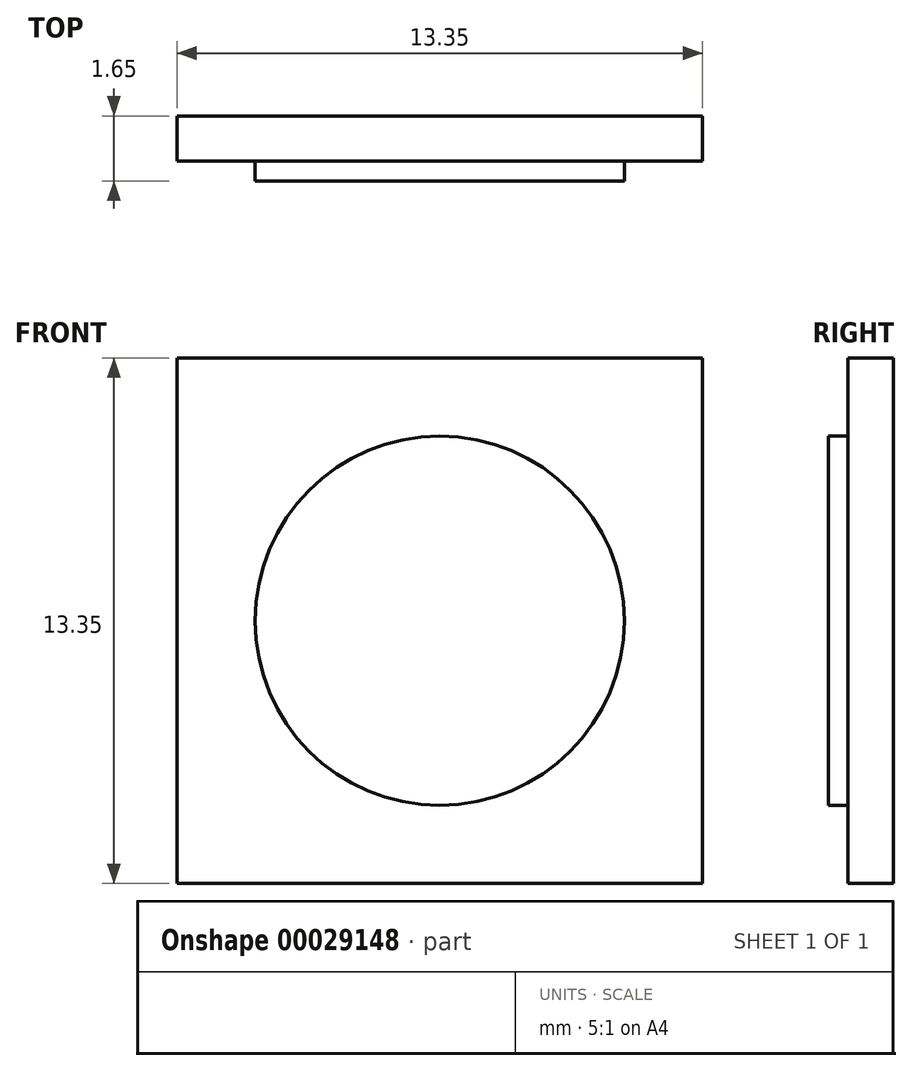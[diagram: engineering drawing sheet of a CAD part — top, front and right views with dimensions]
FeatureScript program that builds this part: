
annotation { "Feature Type Name" : "Feature", "Feature Type Description" : "" }
export const myFeature = defineFeature(function(context is Context, id is Id, definition is map)
    precondition{}
    {
        {
            var Q0;
            Q0=qCreatedBy(makeId("Front.planeOp"),FACE);
            var sketch = newSketch(context, id + "F0", { "sketchPlane" : qUnion([Q0])});
            skLineSegment(sketch, "E0.bottom", {"start": v(0, 0) * mm, "end": v(-13.35, 0) * mm});
            skLineSegment(sketch, "E0.top", {"start": v(0, 13.35) * mm, "end": v(-13.35, 13.35) * mm});
            skLineSegment(sketch, "E0.left", {"start": v(0, 0) * mm, "end": v(0, 13.35) * mm});
            skLineSegment(sketch, "E0.right", {"start": v(-13.35, 0) * mm, "end": v(-13.35, 13.35) * mm});
            skSolve(sketch);
        }
        {
            var Q0;
            Q0 = qSketchRegion(id + "F0", true);
            extrude(context, id + "F1", {"entities" : qUnion([Q0]), "depth" : 1.15 * mm});
        }
        {
            var Q0;
            Q0=makeQuery(id+"F1.opExtrude","CAP_FACE",FACE,{"disambiguationData":[OSD([sQuery(id+"F0.wireOp",EDGE,"E0.bottom"),sQuery(id+"F0.wireOp",EDGE,"E0.top"),sQuery(id+"F0.wireOp",EDGE,"E0.left"),sQuery(id+"F0.wireOp",EDGE,"E0.right")])],"isStart":false});
            var sketch = newSketch(context, id + "F2", { "sketchPlane" : qUnion([Q0])});
            skCircle(sketch, "E1", {"center": v(-6.68, 6.68) * mm, "radius": 4.69 * mm});
            skSolve(sketch);
        }
        {
            var Q0;
            Q0 = qSketchRegion(id + "F2", true);
            extrude(context, id + "F3", {"entities" : qUnion([Q0]), "operationType" : NewBodyOperationType.ADD, "depth" : .5 * mm});
        }
    });
